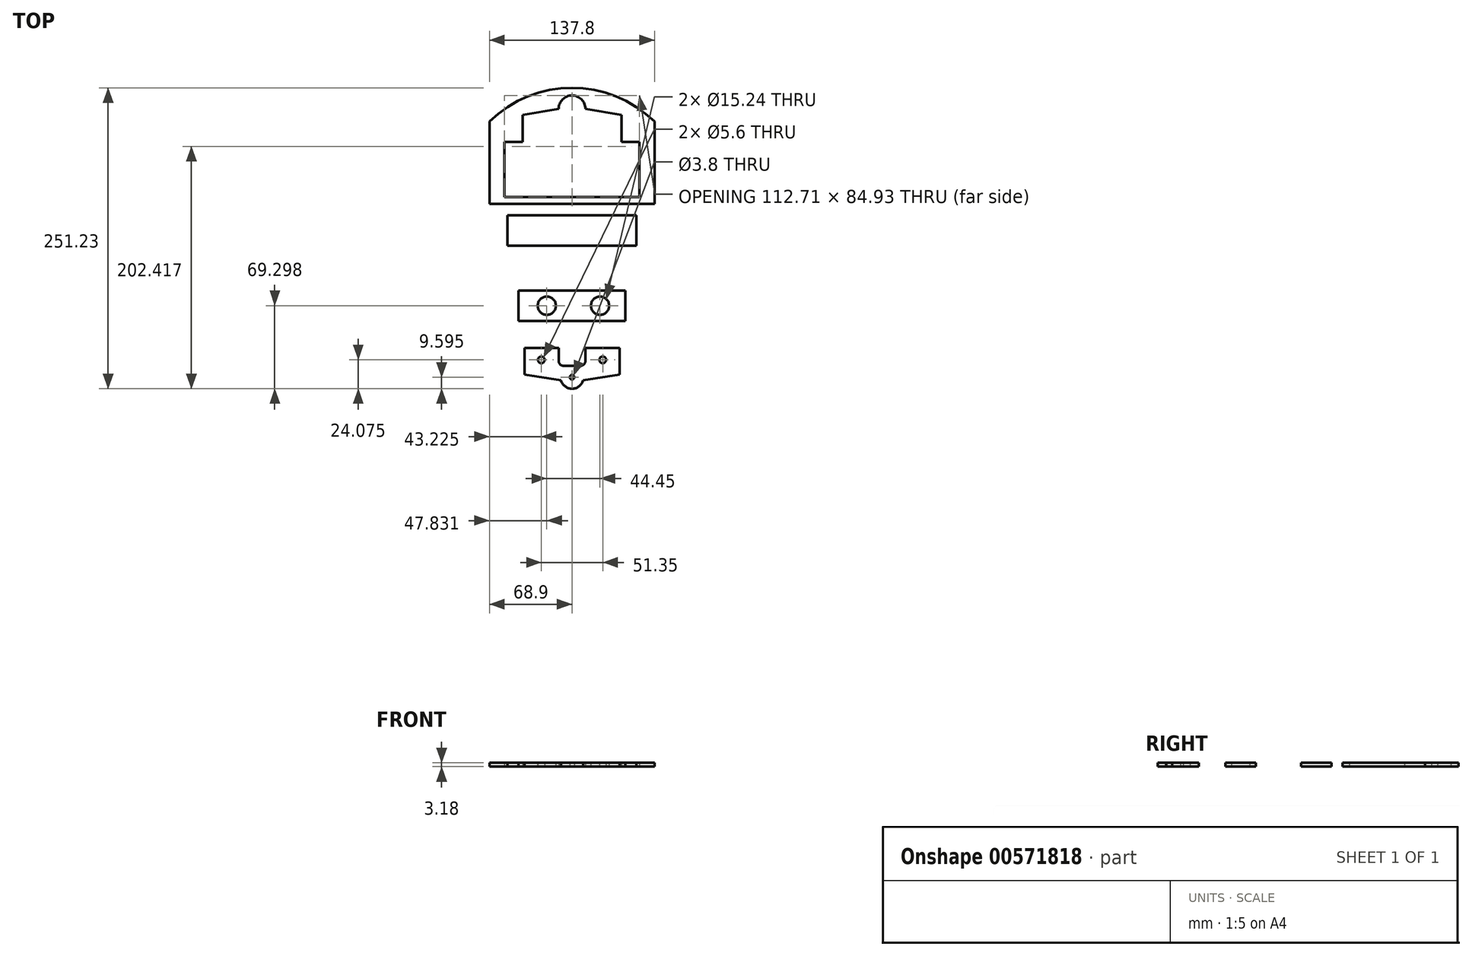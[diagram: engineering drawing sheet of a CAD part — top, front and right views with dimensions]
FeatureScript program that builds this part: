
annotation { "Feature Type Name" : "Feature", "Feature Type Description" : "" }
export const myFeature = defineFeature(function(context is Context, id is Id, definition is map)
    precondition{}
    {
        {
            var Q0;
            Q0=qCreatedBy(makeId("Top.planeOp"),FACE);
            var sketch = newSketch(context, id + "F0", { "sketchPlane" : qUnion([Q0])});
            skArc(sketch, "E0", {"start": v(11.11, 0) * mm, "mid": v(0, 11.11) * mm, "end": v(-11.11, 0) * mm});
            skLineSegment(sketch, "E1.top", {"start": v(68.9, -79.37) * mm, "end": v(-68.9, -79.38) * mm});
            skLineSegment(sketch, "E1.left", {"start": v(68.9, -10.67) * mm, "end": v(68.9, -79.37) * mm});
            skLineSegment(sketch, "E1.right", {"start": v(-68.9, -10.67) * mm, "end": v(-68.9, -79.38) * mm});
            skPoint(sketch, "E1.middle", {"position": v(0, -45.02) * mm});
            skArc(sketch, "E2", {"start": v(68.9, -10.67) * mm, "mid": v(0, 17.46) * mm, "end": v(-68.9, -10.67) * mm});
            skPoint(sketch, "E2.centerSnap0", {"position": v(0, -79.38) * mm});
            skLineSegment(sketch, "E3.bottom", {"start": v(56.36, -73.82) * mm, "end": v(-56.36, -73.82) * mm});
            skLineSegment(sketch, "E3.top", {"start": v(56.36, -27.78) * mm, "end": v(41.28, -27.78) * mm});
            skLineSegment(sketch, "E3.left", {"start": v(56.36, -73.82) * mm, "end": v(56.36, -27.78) * mm});
            skLineSegment(sketch, "E3.right", {"start": v(-56.36, -73.82) * mm, "end": v(-56.36, -27.78) * mm});
            skPoint(sketch, "E3.middle", {"position": v(0, -50.8) * mm});
            skLineSegment(sketch, "E4.left", {"start": v(41.28, -27.78) * mm, "end": v(41.28, -5.08) * mm});
            skLineSegment(sketch, "E4.right", {"start": v(-41.28, -27.78) * mm, "end": v(-41.28, -5.08) * mm});
            skPoint(sketch, "E4.middle", {"position": v(0, -16.43) * mm});
            skLineSegment(sketch, "E5.trimOffspring", {"start": v(-41.28, -27.78) * mm, "end": v(-56.36, -27.78) * mm});
            skLineSegment(sketch, "E6", {"start": v(41.28, -5.08) * mm, "end": v(11.11, 0) * mm});
            skLineSegment(sketch, "E7", {"start": v(-41.28, -5.08) * mm, "end": v(-11.11, 0) * mm});
            skSolve(sketch);
        }
        {
            var Q0;
            Q0=qCreatedBy(makeId("Top.planeOp"),FACE);
            var sketch = newSketch(context, id + "F1", { "sketchPlane" : qUnion([Q0])});
            skLineSegment(sketch, "E8.bottom", {"start": v(53.86, -88.82) * mm, "end": v(-53.86, -88.82) * mm});
            skLineSegment(sketch, "E8.top", {"start": v(53.86, -114.22) * mm, "end": v(-53.86, -114.22) * mm});
            skLineSegment(sketch, "E8.left", {"start": v(53.86, -88.82) * mm, "end": v(53.86, -114.22) * mm});
            skLineSegment(sketch, "E8.right", {"start": v(-53.86, -88.82) * mm, "end": v(-53.86, -114.22) * mm});
            skPoint(sketch, "E8.middle", {"position": v(0, -101.52) * mm});
            skSolve(sketch);
        }
        {
            var Q0;
            Q0=qCreatedBy(makeId("Top.planeOp"),FACE);
            var sketch = newSketch(context, id + "F2", { "sketchPlane" : qUnion([Q0])});
            skLineSegment(sketch, "E9.bottom", {"start": v(44.67, -151.77) * mm, "end": v(-44.67, -151.77) * mm});
            skLineSegment(sketch, "E9.top", {"start": v(44.67, -177.17) * mm, "end": v(-44.67, -177.17) * mm});
            skLineSegment(sketch, "E9.left", {"start": v(44.67, -151.77) * mm, "end": v(44.67, -177.17) * mm});
            skLineSegment(sketch, "E9.right", {"start": v(-44.67, -151.77) * mm, "end": v(-44.67, -177.17) * mm});
            skPoint(sketch, "E9.middle", {"position": v(0, -164.47) * mm});
            skCircle(sketch, "E10", {"center": v(-21.07, -164.47) * mm, "radius": 7.62 * mm});
            skCircle(sketch, "E11", {"center": v(23.38, -164.47) * mm, "radius": 7.62 * mm});
            skSolve(sketch);
        }
        {
            var Q0;
            Q0=qCreatedBy(makeId("Top.planeOp"),FACE);
            var sketch = newSketch(context, id + "F3", { "sketchPlane" : qUnion([Q0])});
            skLineSegment(sketch, "E12.top", {"start": v(39.69, -199.7) * mm, "end": v(11.12, -199.7) * mm});
            skLineSegment(sketch, "E12.left", {"start": v(39.69, -221.91) * mm, "end": v(39.68, -199.7) * mm});
            skLineSegment(sketch, "E12.right", {"start": v(-39.68, -221.91) * mm, "end": v(-39.68, -199.7) * mm});
            skPoint(sketch, "E12.middle", {"position": v(0, -210.8) * mm});
            skLineSegment(sketch, "E13.top", {"start": v(7.12, -214.7) * mm, "end": v(-7.11, -214.7) * mm});
            skLineSegment(sketch, "E13.left", {"start": v(11.11, -199.7) * mm, "end": v(11.12, -210.7) * mm});
            skLineSegment(sketch, "E13.right", {"start": v(-11.12, -199.7) * mm, "end": v(-11.11, -210.7) * mm});
            skPoint(sketch, "E13.middle", {"position": v(0, -207.2) * mm});
            skCircle(sketch, "E14", {"center": v(-25.67, -209.7) * mm, "radius": 2.8 * mm});
            skCircle(sketch, "E15", {"center": v(0, -224.17) * mm, "radius": 1.9 * mm});
            skArc(sketch, "E16", {"start": v(-9.24, -226.78) * mm, "mid": v(0, -233.77) * mm, "end": v(9.24, -226.78) * mm});
            skLineSegment(sketch, "E17", {"start": v(39.69, -221.91) * mm, "end": v(9.24, -226.78) * mm});
            skLineSegment(sketch, "E18", {"start": v(-39.69, -221.91) * mm, "end": v(-9.24, -226.78) * mm});
            skLineSegment(sketch, "E19.trimOffspring", {"start": v(-11.12, -199.7) * mm, "end": v(-39.68, -199.7) * mm});
            skPoint(sketch, "E20.visualSharp", {"position": v(-11.11, -214.7) * mm});
            skArc(sketch, "E20.filletArc", {"start": v(-11.12, -210.7) * mm, "mid": v(-9.94, -213.52) * mm, "end": v(-7.11, -214.7) * mm});
            skPoint(sketch, "E21.visualSharp", {"position": v(11.12, -214.7) * mm});
            skArc(sketch, "E21.filletArc", {"start": v(7.12, -214.7) * mm, "mid": v(9.94, -213.52) * mm, "end": v(11.12, -210.7) * mm});
            skCircle(sketch, "E22.MirrorC", {"center": v(25.67, -209.7) * mm, "radius": 2.8 * mm});
            skSolve(sketch);
        }
        {
            var Q0;
            Q0=makeQuery(id+"F0.imprint","IMPRINT",FACE,{"disambiguationData":[TD([[makeQuery(id+"F0.imprint","IMPRINT",EDGE,{"derivedFrom":sQuery(id+"F0.wireOp",EDGE,"E0")}),-1.0]])]});
            var Q1;
            Q1=makeQuery(id+"F1.imprint","IMPRINT",FACE,{"disambiguationData":[TD([[makeQuery(id+"F1.imprint","IMPRINT",EDGE,{"derivedFrom":sQuery(id+"F1.wireOp",EDGE,"E8.bottom")}),1.0]])]});
            var Q2;
            Q2=makeQuery(id+"F2.imprint","IMPRINT",FACE,{"disambiguationData":[TD([[makeQuery(id+"F2.imprint","IMPRINT",EDGE,{"derivedFrom":sQuery(id+"F2.wireOp",EDGE,"E9.bottom")}),1.0]])]});
            var Q3;
            Q3=makeQuery(id+"F3.imprint","IMPRINT",FACE,{"disambiguationData":[TD([[makeQuery(id+"F3.imprint","IMPRINT",EDGE,{"derivedFrom":sQuery(id+"F3.wireOp",EDGE,"E12.top")}),1.0]])]});
            extrude(context, id + "F4", {"entities" : qUnion([Q0, Q1, Q2, Q3]), "depth" : 3.17 * mm, "offsetDistance" : 25.4 * mm});
        }
    });
